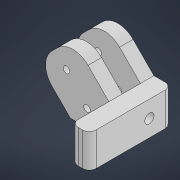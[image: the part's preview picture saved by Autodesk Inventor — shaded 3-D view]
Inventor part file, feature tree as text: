
AUTODESK INVENTOR PART (.ipt)
format: ipt  version: 2022 (Build 260153000, 153)  size: 231,936 bytes
history: native  units: in
note: dims shown in document units (in); Inventor stores cm internally (conversion verified against a paired STEP export)
features: projected_geometry x9, sketch x6, plane x2, hole x2, extrude x2, mirror x1, fillet x1
ambient origin geometry x8: Origin, YZ Plane, XZ Plane, XY Plane, X Axis, Y Axis, Z Axis, Center Point
bodies: Body1 (feature_tree)
feature tree (23):
  plane  "Work Plane1"
  hole  "Hole1"  [1 undecoded]
  extrude  "Extrusion4"  Depth=0.1575in
  extrude  "Extrusion5"  Depth=0.0787in
  plane  "Work Plane2"
  mirror  "Mirror1"
  fillet  "Fillet1"  Radius=0.0787in
  hole  "Hole5"  [1 undecoded]
  sketch  "Sketch1"  dims[d0=-0.2559in d1=0.5118in d2=0.0in]
  sketch  "Sketch3"  dims[d5=0.0996in d6=0.2362in d7=0.1575in d8=0.0787in d9=90.0deg d10=0.315in d11=0.8108in]
  sketch  "Sketch5"  dims[d19=0.0996in d20=0.2362in d21=0.1575in d22=0.0787in d23=90.0deg d24=0.315in d25=0.8108in d26=0.3543in]
  sketch  "Sketch6"  dims[d27=0.3543in d28=0.0787in d29=0.0787in]
  projected_geometry  "Projected Loop1"
  projected_geometry  "Projected Loop2"
  sketch  "Sketch7"  dims[d30=0.0394in d31=0.3937in d32=0.0in]
  projected_geometry  "Projected Loop3"
  projected_geometry  "Projected Loop4"
  projected_geometry  "Projected Loop5"
  projected_geometry  "Projected Loop6"
  projected_geometry  "Projected Loop7"
  projected_geometry  "Projected Loop8"
  sketch  "Sketch8"  dims[d33=0.5906in d34=0.0in d35=0.2756in d36=0.2756in d37=0.4872in d38=0.2067in d39=0.5748in d40=0.3287in d41=0.1417in d42=0.2362in d43=0.2559in d44=0.1181in d45=0.6181in d46=0.3937in d47=0.0in]
  projected_geometry  "Projected Loop11"
note: 2 required parameter values undecoded (feature->parameter linkage not recoverable at this tier; creation-order binding heuristic only, values carry confidence <= 0.55)
